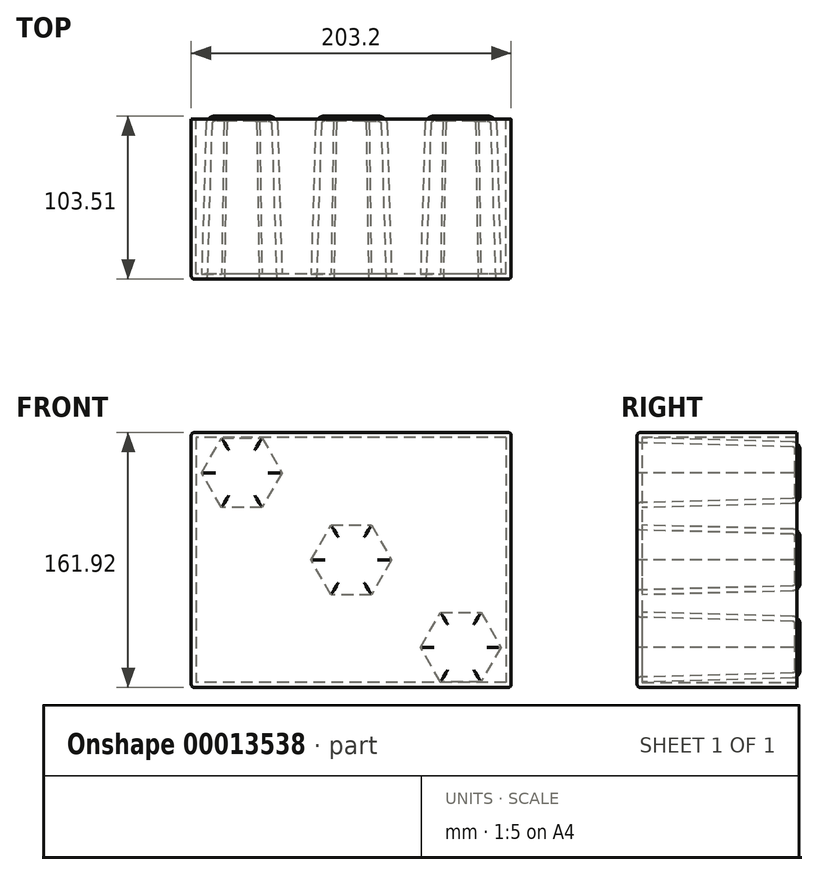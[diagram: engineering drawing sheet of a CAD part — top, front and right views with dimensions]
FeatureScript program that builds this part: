
annotation { "Feature Type Name" : "Feature", "Feature Type Description" : "" }
export const myFeature = defineFeature(function(context is Context, id is Id, definition is map)
    precondition{}
    {
        {
            var Q0;
            Q0=qCreatedBy(makeId("Front.planeOp"),FACE);
            var sketch = newSketch(context, id + "F0", { "sketchPlane" : qUnion([Q0])});
            skLineSegment(sketch, "E0.rect.bottom", {"start": v(101.6, 80.96) * mm, "end": v(-101.6, 80.96) * mm});
            skLineSegment(sketch, "E0.rect.top", {"start": v(101.6, -80.96) * mm, "end": v(-101.6, -80.96) * mm});
            skLineSegment(sketch, "E0.rect.left", {"start": v(101.6, 80.96) * mm, "end": v(101.6, -80.96) * mm});
            skLineSegment(sketch, "E0.rect.right", {"start": v(-101.6, 80.96) * mm, "end": v(-101.6, -80.96) * mm});
            skPoint(sketch, "E0.rect.middle", {"position": v(0, 0) * mm});
            skSolve(sketch);
        }
        {
            var Q0;
            Q0 = qSketchRegion(id + "F0", true);
            extrude(context, id + "F1", {"entities" : qUnion([Q0]), "depth" : 101.6 * mm});
        }
        {
            var Q0;
            Q0=makeQuery(id+"F1.opExtrude","CAP_FACE",FACE,{"disambiguationData":[OSD([sQuery(id+"F0.wireOp",EDGE,"E0.rect.bottom"),sQuery(id+"F0.wireOp",EDGE,"E0.rect.top"),sQuery(id+"F0.wireOp",EDGE,"E0.rect.left"),sQuery(id+"F0.wireOp",EDGE,"E0.rect.right")])],"isStart":false});
            var sketch = newSketch(context, id + "F2", { "sketchPlane" : qUnion([Q0])});
            skCircle(sketch, "E1.cCircle", {"center": v(-69.53, 55.4) * mm, "radius": 19.05 * mm, "construction": true});
            skLineSegment(sketch, "E1.0", {"start": v(-47.53, 55.4) * mm, "end": v(-58.53, 36.35) * mm});
            skLineSegment(sketch, "E1.1", {"start": v(-58.53, 36.35) * mm, "end": v(-80.52, 36.35) * mm});
            skLineSegment(sketch, "E1.2", {"start": v(-80.52, 36.35) * mm, "end": v(-91.52, 55.4) * mm});
            skLineSegment(sketch, "E1.3", {"start": v(-91.52, 55.4) * mm, "end": v(-80.52, 74.45) * mm});
            skLineSegment(sketch, "E1.4", {"start": v(-80.52, 74.45) * mm, "end": v(-58.53, 74.45) * mm});
            skLineSegment(sketch, "E1.5", {"start": v(-58.53, 74.45) * mm, "end": v(-47.53, 55.4) * mm});
            skPoint(sketch, "E1.0.midPoint", {"position": v(-53.03, 45.88) * mm});
            skCircle(sketch, "E2.cCircle", {"center": v(0, 0) * mm, "radius": 19.05 * mm, "construction": true});
            skLineSegment(sketch, "E2.0", {"start": v(22, 0) * mm, "end": v(11, -19.05) * mm});
            skLineSegment(sketch, "E2.1", {"start": v(11, -19.05) * mm, "end": v(-11, -19.05) * mm});
            skLineSegment(sketch, "E2.2", {"start": v(-11, -19.05) * mm, "end": v(-22, 0) * mm});
            skLineSegment(sketch, "E2.3", {"start": v(-22, 0) * mm, "end": v(-11, 19.05) * mm});
            skLineSegment(sketch, "E2.4", {"start": v(-11, 19.05) * mm, "end": v(11, 19.05) * mm});
            skLineSegment(sketch, "E2.5", {"start": v(11, 19.05) * mm, "end": v(22, 0) * mm});
            skPoint(sketch, "E2.0.midPoint", {"position": v(16.5, -9.53) * mm});
            skCircle(sketch, "E3.cCircle", {"center": v(69.53, -55.4) * mm, "radius": 19.05 * mm, "construction": true});
            skLineSegment(sketch, "E3.0", {"start": v(91.52, -55.4) * mm, "end": v(80.52, -74.45) * mm});
            skLineSegment(sketch, "E3.1", {"start": v(80.52, -74.45) * mm, "end": v(58.53, -74.45) * mm});
            skLineSegment(sketch, "E3.2", {"start": v(58.53, -74.45) * mm, "end": v(47.53, -55.4) * mm});
            skLineSegment(sketch, "E3.3", {"start": v(47.53, -55.4) * mm, "end": v(58.53, -36.35) * mm});
            skLineSegment(sketch, "E3.4", {"start": v(58.53, -36.35) * mm, "end": v(80.52, -36.35) * mm});
            skLineSegment(sketch, "E3.5", {"start": v(80.52, -36.35) * mm, "end": v(91.52, -55.4) * mm});
            skPoint(sketch, "E3.0.midPoint", {"position": v(86.02, -64.93) * mm});
            skLineSegment(sketch, "E4", {"start": v(-101.6, 80.96) * mm, "end": v(101.6, -80.96) * mm});
            skSolve(sketch);
        }
        {
            var Q0;
            Q0 = qSketchRegion(id + "F2", true);
            extrude(context, id + "F3", {"entities" : qUnion([Q0]), "operationType" : NewBodyOperationType.REMOVE, "oppositeDirection" : true, "depth" : 100.33 * mm, "hasDraft" : true, "draftAngle" : 1.5 * degree, "draftPullDirection" : true});
        }
        {
            var Q0;
            Q0=makeQuery(id+"F1.opExtrude","CAP_FACE",FACE,{"disambiguationData":[OSD([sQuery(id+"F0.wireOp",EDGE,"E0.rect.bottom"),sQuery(id+"F0.wireOp",EDGE,"E0.rect.top"),sQuery(id+"F0.wireOp",EDGE,"E0.rect.left"),sQuery(id+"F0.wireOp",EDGE,"E0.rect.right")])],"isStart":false});
            var Q1;
            Q1=makeQuery(id+"F3.boolean.opBoolean","COPY",FACE,{"derivedFrom":makeQuery(id+"F3.opExtrude","CAP_FACE",FACE,{"disambiguationData":[OSD([sQuery(id+"F2.wireOp",EDGE,"E1.0"),sQuery(id+"F2.wireOp",EDGE,"E1.1"),sQuery(id+"F2.wireOp",EDGE,"E1.2"),sQuery(id+"F2.wireOp",EDGE,"E1.3"),sQuery(id+"F2.wireOp",EDGE,"E1.4"),sQuery(id+"F2.wireOp",EDGE,"E1.5")])],"isStart":false})});
            var Q2;
            Q2=makeQuery(id+"F3.boolean.opBoolean","COPY",FACE,{"derivedFrom":makeQuery(id+"F3.opExtrude","CAP_FACE",FACE,{"disambiguationData":[OSD([sQuery(id+"F2.wireOp",EDGE,"E2.0"),sQuery(id+"F2.wireOp",EDGE,"E2.1"),sQuery(id+"F2.wireOp",EDGE,"E2.2"),sQuery(id+"F2.wireOp",EDGE,"E2.3"),sQuery(id+"F2.wireOp",EDGE,"E2.4"),sQuery(id+"F2.wireOp",EDGE,"E2.5")])],"isStart":false})});
            var Q3;
            Q3=makeQuery(id+"F3.boolean.opBoolean","COPY",FACE,{"derivedFrom":makeQuery(id+"F3.opExtrude","CAP_FACE",FACE,{"disambiguationData":[OSD([sQuery(id+"F2.wireOp",EDGE,"E3.0"),sQuery(id+"F2.wireOp",EDGE,"E3.1"),sQuery(id+"F2.wireOp",EDGE,"E3.2"),sQuery(id+"F2.wireOp",EDGE,"E3.3"),sQuery(id+"F2.wireOp",EDGE,"E3.4"),sQuery(id+"F2.wireOp",EDGE,"E3.5")])],"isStart":false})});
            var Q4;
            Q4=makeQuery(id+"F1.opExtrude","SWEPT_EDGE",EDGE,{"disambiguationData":[OSD([sQuery(id+"F0.wireOp",EDGE,"E0.rect.bottom"),sQuery(id+"F0.wireOp",EDGE,"E0.rect.right")])]});
            var Q5;
            Q5=makeQuery(id+"F1.opExtrude","SWEPT_EDGE",EDGE,{"disambiguationData":[OSD([sQuery(id+"F0.wireOp",EDGE,"E0.rect.bottom"),sQuery(id+"F0.wireOp",EDGE,"E0.rect.left")])]});
            var Q6;
            Q6=makeQuery(id+"F1.opExtrude","SWEPT_EDGE",EDGE,{"disambiguationData":[OSD([sQuery(id+"F0.wireOp",EDGE,"E0.rect.top"),sQuery(id+"F0.wireOp",EDGE,"E0.rect.left")])]});
            var Q7;
            Q7=makeQuery(id+"F1.opExtrude","SWEPT_EDGE",EDGE,{"disambiguationData":[OSD([sQuery(id+"F0.wireOp",EDGE,"E0.rect.top"),sQuery(id+"F0.wireOp",EDGE,"E0.rect.right")])]});
            fillet(context, id + "F4", {"entities" : qUnion([Q0, Q1, Q2, Q3, Q4, Q5, Q6, Q7]), "radius" : 1.9 * mm, "tangentPropagation" : true, "allowEdgeOverflow" : false});
        }
        {
            var Q0;
            Q0=makeQuery(id+"F1.opExtrude","CAP_FACE",FACE,{"disambiguationData":[OSD([sQuery(id+"F0.wireOp",EDGE,"E0.rect.bottom"),sQuery(id+"F0.wireOp",EDGE,"E0.rect.top"),sQuery(id+"F0.wireOp",EDGE,"E0.rect.left"),sQuery(id+"F0.wireOp",EDGE,"E0.rect.right")])],"isStart":true});
            shell(context, id + "F5", {"entities" : qUnion([Q0]), "thickness" : 3.17 * mm});
        }
    });
